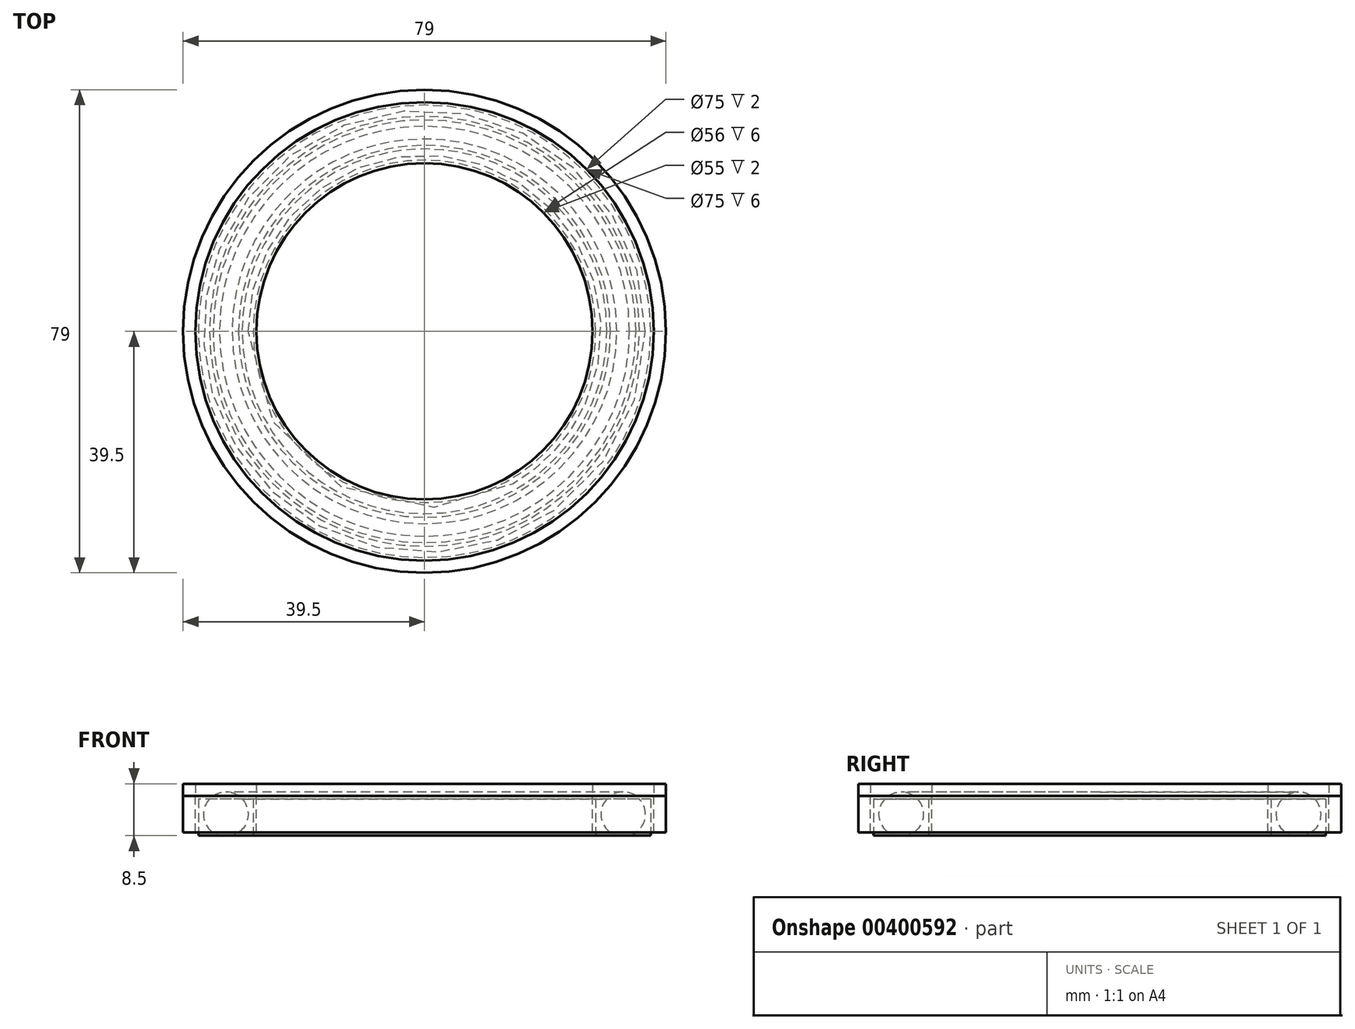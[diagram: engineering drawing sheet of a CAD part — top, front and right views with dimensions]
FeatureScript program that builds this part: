
annotation { "Feature Type Name" : "Feature", "Feature Type Description" : "" }
export const myFeature = defineFeature(function(context is Context, id is Id, definition is map)
    precondition{}
    {
        {
            var Q0;
            Q0=qCreatedBy(makeId("Top.planeOp"),FACE);
            var sketch = newSketch(context, id + "F0", { "sketchPlane" : qUnion([Q0])});
            skCircle(sketch, "E0", {"center": v(0, 0) * mm, "radius": 35 * mm});
            skCircle(sketch, "E1.0", {"center": v(0, 0) * mm, "radius": 30 * mm});
            skLineSegment(sketch, "E2", {"start": v(30, 0) * mm, "end": v(35, 0) * mm});
            skCircle(sketch, "E3.0", {"center": v(0, 0) * mm, "radius": 37 * mm});
            skCircle(sketch, "E4.0", {"center": v(0, 0) * mm, "radius": 28 * mm});
            skSolve(sketch);
        }
        {
            var Q0;
            Q0=makeQuery(id+"F0.imprint","IMPRINT",FACE,{"disambiguationData":[TD([[makeQuery(id+"F0.imprint","IMPRINT",EDGE,{"derivedFrom":sQuery(id+"F0.wireOp",EDGE,"E0")}),1.0]])]});
            var Q1;
            Q1=makeQuery(id+"F0.imprint","IMPRINT",FACE,{"disambiguationData":[TD([[makeQuery(id+"F0.imprint","IMPRINT",EDGE,{"derivedFrom":sQuery(id+"F0.wireOp",EDGE,"E1.0")}),1.0]])]});
            var Q2;
            Q2=makeQuery(id+"F0.imprint","IMPRINT",FACE,{"disambiguationData":[TD([[makeQuery(id+"F0.imprint","IMPRINT",EDGE,{"derivedFrom":sQuery(id+"F0.wireOp",EDGE,"E0")}),-1.0]])]});
            extrude(context, id + "F1", {"entities" : qUnion([Q0, Q1, Q2]), "depth" : 6 * mm});
        }
        {
            var Q0;
            Q0=qCreatedBy(makeId("Front.planeOp"),FACE);
            var sketch = newSketch(context, id + "F2", { "sketchPlane" : qUnion([Q0])});
            skLineSegment(sketch, "E5.0", {"start": v(-37, 0) * mm, "end": v(37, 0) * mm});
            skLineSegment(sketch, "E6", {"start": v(37, 0) * mm, "end": v(37, 7) * mm});
            skCircle(sketch, "E7", {"center": v(32.5, 3.5) * mm, "radius": 3.5 * mm});
            skLineSegment(sketch, "E8", {"start": v(0, 0) * mm, "end": v(0, 7) * mm, "construction": true});
            skLineSegment(sketch, "E9", {"start": v(32.5, 7) * mm, "end": v(32.5, 0) * mm});
            skCircle(sketch, "E10.MirrorC", {"center": v(-32.5, 3.5) * mm, "radius": 3.5 * mm});
            skSolve(sketch);
        }
        {
            var Q0;
            Q0=qCreatedBy(makeId("Front.planeOp"),FACE);
            var sketch = newSketch(context, id + "F3", { "sketchPlane" : qUnion([Q0])});
            skCircle(sketch, "E11.0", {"center": v(32.5, 3.5) * mm, "radius": 3.5 * mm, "construction": true});
            skCircle(sketch, "E12.0", {"center": v(32.5, 3.5) * mm, "radius": 3.65 * mm});
            skSolve(sketch);
        }
        {
            var Q0;
            Q0=makeQuery(id+"F3.imprint","IMPRINT",FACE,{"disambiguationData":[TD([[makeQuery(id+"F3.imprint","IMPRINT",EDGE,{"derivedFrom":sQuery(id+"F3.wireOp",EDGE,"E12.0")}),1.0]])]});
            var Q1;
            Q1=sQuery(id+"F2.wireOp",EDGE,"E8");
            revolve(context, id + "F4", {"operationType" : NewBodyOperationType.REMOVE, "entities" : qUnion([Q0]), "axis" : qUnion([Q1]), "revolveType" : RevolveType.FULL, "oppositeDirection" : true});
        }
        {
            var Q0;
            {var subQ0=sQuery(id+"F2.wireOp",EDGE,"E9");Q0=makeQuery(id+"F2.imprint","IMPRINT",FACE,{"disambiguationData":[TD([[makeQuery(id+"F2.imprint","IMPRINT",EDGE,{"derivedFrom":subQ0}),1.0]])]});}
            var Q1;
            Q1=sQuery(id+"F2.wireOp",EDGE,"E9");
            revolve(context, id + "F5", {"entities" : qUnion([Q0]), "axis" : qUnion([Q1]), "revolveType" : RevolveType.FULL});
        }
        {
            var Q0;
            Q0=makeQuery(id+"F5.opRevolve","SWEPT_BODY",BODY,{"disambiguationData":[OSD([sQuery(id+"F2.wireOp",EDGE,"E7"),sQuery(id+"F2.wireOp",EDGE,"E9")])]});
            var Q1;
            Q1=sQuery(id+"F2.wireOp",EDGE,"E8");
            circularPattern(context, id + "F6", {"entities" : qUnion([Q0]), "axis" : qUnion([Q1]), "angle" : 360 * degree, "instanceCount" : 29, "equalSpace" : true});
        }
        {
            var Q0;
            {var subQ0=sQuery(id+"F0.wireOp",EDGE,"E3.0");Q0=makeQuery(id+"F4.boolean.opBoolean","SPLIT",FACE,{"disambiguationData":[TD([makeQuery(id+"F1.opExtrude","SWEPT_FACE",FACE,{"disambiguationData":[OSD([subQ0])]})])],"derivedFrom":makeQuery(id+"F1.opExtrude","CAP_FACE",FACE,{"disambiguationData":[OSD([subQ0,sQuery(id+"F0.wireOp",EDGE,"E4.0")])],"isStart":false})});}
            cPlane(context, id + "F7", {"entities" : qUnion([Q0]), "cplaneType" : CPlaneType.OFFSET, "offset" : .5 * mm, "width" : 150 * mm, "height" : 150 * mm});
        }
        {
            var Q0;
            Q0=qCreatedBy(id+"F7.planeOp",FACE);
            var sketch = newSketch(context, id + "F8", { "sketchPlane" : qUnion([Q0])});
            skCircle(sketch, "E13.0", {"center": v(0, 0) * mm, "radius": 37 * mm, "construction": true});
            skCircle(sketch, "E14.0", {"center": v(0, 0) * mm, "radius": 28 * mm, "construction": true});
            skCircle(sketch, "E15.0", {"center": v(0, 0) * mm, "radius": 27.5 * mm});
            skCircle(sketch, "E16.0", {"center": v(0, 0) * mm, "radius": 37.5 * mm});
            skCircle(sketch, "E17.0", {"center": v(0, 0) * mm, "radius": 39.5 * mm});
            skSolve(sketch);
        }
        {
            var Q0;
            Q0=makeQuery(id+"F8.imprint","IMPRINT",FACE,{"disambiguationData":[TD([[makeQuery(id+"F8.imprint","IMPRINT",EDGE,{"derivedFrom":sQuery(id+"F8.wireOp",EDGE,"E16.0")}),-1.0]])]});
            var Q1;
            Q1=makeQuery(id+"F8.imprint","IMPRINT",FACE,{"disambiguationData":[TD([[makeQuery(id+"F8.imprint","IMPRINT",EDGE,{"derivedFrom":sQuery(id+"F8.wireOp",EDGE,"E15.0")}),1.0]])]});
            var Q2;
            {var subQ0=sQuery(id+"F0.wireOp",EDGE,"E4.0");Q2=makeQuery(id+"F4.boolean.opBoolean","SPLIT",FACE,{"disambiguationData":[TD([makeQuery(id+"F1.opExtrude","SWEPT_FACE",FACE,{"disambiguationData":[OSD([subQ0])]})])],"derivedFrom":makeQuery(id+"F1.opExtrude","CAP_FACE",FACE,{"disambiguationData":[OSD([sQuery(id+"F0.wireOp",EDGE,"E3.0"),subQ0])],"isStart":true})});}
            extrude(context, id + "F9", {"entities" : qUnion([Q0, Q1]), "oppositeDirection" : true, "endBoundEntityFace" : qUnion([Q2]), "depth" : 6 * mm});
        }
        {
            var Q0;
            Q0=makeQuery(id+"F8.imprint","IMPRINT",FACE,{"disambiguationData":[TD([[makeQuery(id+"F8.imprint","IMPRINT",EDGE,{"derivedFrom":sQuery(id+"F8.wireOp",EDGE,"E15.0")}),-1.0]])]});
            var Q1;
            Q1=makeQuery(id+"F9.opExtrude","CAP_FACE",FACE,{"disambiguationData":[OSD([sQuery(id+"F8.wireOp",EDGE,"E16.0"),sQuery(id+"F8.wireOp",EDGE,"E17.0")])],"isStart":true});
            var Q2;
            Q2=makeQuery(id+"F9.opExtrude","CAP_FACE",FACE,{"disambiguationData":[OSD([sQuery(id+"F8.wireOp",EDGE,"E15.0")])],"isStart":true});
            extrude(context, id + "F10", {"entities" : qUnion([Q0, Q1, Q2]), "depth" : 2 * mm});
        }
        {
            var Q0;
            Q0=makeQuery(id+"F3.imprint","IMPRINT",FACE,{"disambiguationData":[TD([[makeQuery(id+"F3.imprint","IMPRINT",EDGE,{"derivedFrom":sQuery(id+"F3.wireOp",EDGE,"E12.0")}),1.0]])]});
            var Q1;
            Q1=sQuery(id+"F2.wireOp",EDGE,"E8");
            revolve(context, id + "F11", {"operationType" : NewBodyOperationType.REMOVE, "entities" : qUnion([Q0]), "axis" : qUnion([Q1]), "revolveType" : RevolveType.FULL, "oppositeDirection" : true});
        }
    });
